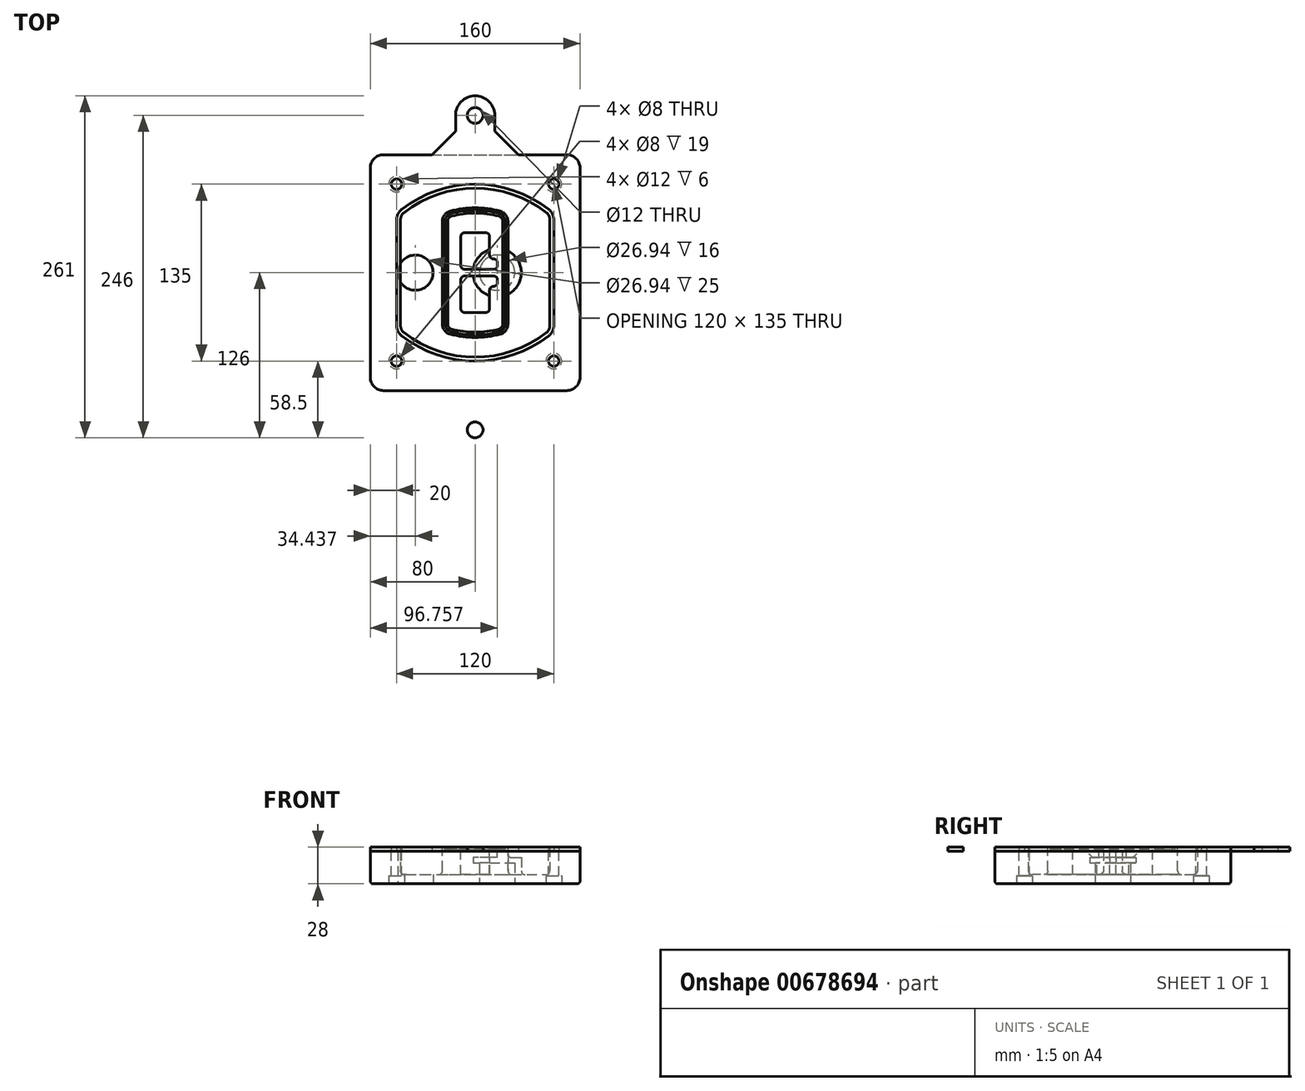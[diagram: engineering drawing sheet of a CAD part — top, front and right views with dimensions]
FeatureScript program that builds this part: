
annotation { "Feature Type Name" : "Feature", "Feature Type Description" : "" }
export const myFeature = defineFeature(function(context is Context, id is Id, definition is map)
    precondition{}
    {
        {
            var Q0;
            Q0=qCreatedBy(makeId("Top.planeOp"),FACE);
            var sketch = newSketch(context, id + "F0", { "sketchPlane" : qUnion([Q0])});
            skPoint(sketch, "E0.rect.middle", {"position": v(0, 0) * mm});
            skLineSegment(sketch, "E1.bottom", {"start": v(-70, -90) * mm, "end": v(70, -90) * mm});
            skLineSegment(sketch, "E1.top", {"start": v(-70, 90) * mm, "end": v(70, 90) * mm});
            skLineSegment(sketch, "E1.left", {"start": v(-80, -80) * mm, "end": v(-80, 80) * mm});
            skLineSegment(sketch, "E1.right", {"start": v(80, -80) * mm, "end": v(80, 80) * mm});
            skLineSegment(sketch, "E2", {"start": v(-80, 90) * mm, "end": v(80, -90) * mm, "construction": true});
            skLineSegment(sketch, "E3", {"start": v(80, 90) * mm, "end": v(-80, -90) * mm, "construction": true});
            skCircle(sketch, "E4", {"center": v(-60, 67.5) * mm, "radius": 4 * mm});
            skCircle(sketch, "E5", {"center": v(60, 67.5) * mm, "radius": 4 * mm});
            skCircle(sketch, "E6", {"center": v(60, -67.5) * mm, "radius": 4 * mm});
            skCircle(sketch, "E7", {"center": v(-60, -67.5) * mm, "radius": 4 * mm});
            skLineSegment(sketch, "E8", {"start": v(-60, 67.5) * mm, "end": v(60, 67.5) * mm, "construction": true});
            skLineSegment(sketch, "E9", {"start": v(60, 67.5) * mm, "end": v(60, -67.5) * mm, "construction": true});
            skLineSegment(sketch, "E10", {"start": v(60, -67.5) * mm, "end": v(-60, -67.5) * mm, "construction": true});
            skLineSegment(sketch, "E11", {"start": v(-60, -67.5) * mm, "end": v(-60, 67.5) * mm, "construction": true});
            skLineSegment(sketch, "E12", {"start": v(-60, 40.3) * mm, "end": v(-60, -40.3) * mm});
            skLineSegment(sketch, "E13", {"start": v(60, 40.3) * mm, "end": v(60, -40.3) * mm});
            skArc(sketch, "E14", {"start": v(56.15, 48.18) * mm, "mid": v(0, 67.5) * mm, "end": v(-56.15, 48.18) * mm});
            skArc(sketch, "E15", {"start": v(-56.15, -48.18) * mm, "mid": v(0, -67.5) * mm, "end": v(56.15, -48.18) * mm});
            skLineSegment(sketch, "E16", {"start": v(-60, 0) * mm, "end": v(60, 0) * mm, "construction": true});
            skPoint(sketch, "E17.visualSharp", {"position": v(-60, -45) * mm});
            skArc(sketch, "E17.filletArc", {"start": v(-60, -40.3) * mm, "mid": v(-58.99, -44.68) * mm, "end": v(-56.15, -48.18) * mm});
            skPoint(sketch, "E18.visualSharp", {"position": v(-60, 45) * mm});
            skArc(sketch, "E18.filletArc", {"start": v(-56.15, 48.18) * mm, "mid": v(-58.99, 44.68) * mm, "end": v(-60, 40.3) * mm});
            skPoint(sketch, "E19.visualSharp", {"position": v(60, 45) * mm});
            skArc(sketch, "E19.filletArc", {"start": v(60, 40.3) * mm, "mid": v(58.99, 44.68) * mm, "end": v(56.15, 48.18) * mm});
            skPoint(sketch, "E20.visualSharp", {"position": v(60, -45) * mm});
            skArc(sketch, "E20.filletArc", {"start": v(56.15, -48.18) * mm, "mid": v(58.99, -44.68) * mm, "end": v(60, -40.3) * mm});
            skPoint(sketch, "E21.visualSharp", {"position": v(-80, 90) * mm});
            skArc(sketch, "E21.filletArc", {"start": v(-70, 90) * mm, "mid": v(-77.07, 87.07) * mm, "end": v(-80, 80) * mm});
            skPoint(sketch, "E22.visualSharp", {"position": v(80, 90) * mm});
            skArc(sketch, "E22.filletArc", {"start": v(80, 80) * mm, "mid": v(77.07, 87.07) * mm, "end": v(70, 90) * mm});
            skPoint(sketch, "E23.visualSharp", {"position": v(80, -90) * mm});
            skArc(sketch, "E23.filletArc", {"start": v(70, -90) * mm, "mid": v(77.07, -87.07) * mm, "end": v(80, -80) * mm});
            skPoint(sketch, "E24.visualSharp", {"position": v(-80, -90) * mm});
            skArc(sketch, "E24.filletArc", {"start": v(-80, -80) * mm, "mid": v(-77.07, -87.07) * mm, "end": v(-70, -90) * mm});
            skArc(sketch, "E25.0", {"start": v(57, 40.3) * mm, "mid": v(56.3, 43.36) * mm, "end": v(54.3, 45.81) * mm});
            skLineSegment(sketch, "E25.1", {"start": v(57, 40.3) * mm, "end": v(57, -40.3) * mm});
            skArc(sketch, "E25.2", {"start": v(54.3, -45.81) * mm, "mid": v(56.3, -43.36) * mm, "end": v(57, -40.3) * mm});
            skArc(sketch, "E25.3", {"start": v(-54.3, -45.81) * mm, "mid": v(0, -64.5) * mm, "end": v(54.3, -45.81) * mm});
            skArc(sketch, "E25.4", {"start": v(-57, -40.3) * mm, "mid": v(-56.3, -43.36) * mm, "end": v(-54.3, -45.81) * mm});
            skArc(sketch, "E25.5", {"start": v(54.3, 45.81) * mm, "mid": v(0, 64.5) * mm, "end": v(-54.3, 45.81) * mm});
            skLineSegment(sketch, "E25.6", {"start": v(-57, 40.3) * mm, "end": v(-57, -40.3) * mm});
            skArc(sketch, "E25.7", {"start": v(-54.3, 45.81) * mm, "mid": v(-56.3, 43.36) * mm, "end": v(-57, 40.3) * mm});
            skArc(sketch, "E26.0", {"start": v(-58.62, 51.33) * mm, "mid": v(-62.58, 46.43) * mm, "end": v(-64, 40.3) * mm});
            skArc(sketch, "E26.1", {"start": v(58.62, 51.33) * mm, "mid": v(0, 71.5) * mm, "end": v(-58.62, 51.33) * mm});
            skArc(sketch, "E26.2", {"start": v(64, 40.3) * mm, "mid": v(62.58, 46.43) * mm, "end": v(58.62, 51.33) * mm});
            skLineSegment(sketch, "E26.3", {"start": v(64, 40.3) * mm, "end": v(64, -40.3) * mm});
            skArc(sketch, "E26.4", {"start": v(58.62, -51.33) * mm, "mid": v(62.58, -46.43) * mm, "end": v(64, -40.3) * mm});
            skLineSegment(sketch, "E26.5", {"start": v(-64, 40.3) * mm, "end": v(-64, -40.3) * mm});
            skArc(sketch, "E26.6", {"start": v(-58.62, -51.33) * mm, "mid": v(0, -71.5) * mm, "end": v(58.62, -51.33) * mm});
            skArc(sketch, "E26.7", {"start": v(-64, -40.3) * mm, "mid": v(-62.58, -46.43) * mm, "end": v(-58.62, -51.33) * mm});
            skSolve(sketch);
        }
        {
            var Q0;
            Q0=makeQuery(id+"F0.imprint","IMPRINT",FACE,{"disambiguationData":[TD([[makeQuery(id+"F0.imprint","IMPRINT",EDGE,{"derivedFrom":sQuery(id+"F0.wireOp",EDGE,"E1.bottom")}),1.0]])]});
            var Q1;
            Q1=makeQuery(id+"F0.imprint","IMPRINT",FACE,{"disambiguationData":[TD([[makeQuery(id+"F0.imprint","IMPRINT",EDGE,{"derivedFrom":sQuery(id+"F0.wireOp",EDGE,"E12")}),1.0]])]});
            var Q2;
            Q2=makeQuery(id+"F0.imprint","IMPRINT",FACE,{"disambiguationData":[TD([[makeQuery(id+"F0.imprint","IMPRINT",EDGE,{"derivedFrom":sQuery(id+"F0.wireOp",EDGE,"E25.0")}),1.0]])]});
            var Q3;
            Q3=makeQuery(id+"F0.imprint","IMPRINT",FACE,{"disambiguationData":[TD([[makeQuery(id+"F0.imprint","IMPRINT",EDGE,{"derivedFrom":sQuery(id+"F0.wireOp",EDGE,"E12")}),-1.0]])]});
            extrude(context, id + "F1", {"entities" : qUnion([Q0, Q1, Q2, Q3]), "oppositeDirection" : true, "depth" : 25 * mm});
        }
        {
            var Q0;
            Q0=makeQuery(id+"F0.imprint","IMPRINT",FACE,{"disambiguationData":[TD([[makeQuery(id+"F0.imprint","IMPRINT",EDGE,{"derivedFrom":sQuery(id+"F0.wireOp",EDGE,"E12")}),1.0]])]});
            extrude(context, id + "F2", {"entities" : qUnion([Q0]), "operationType" : NewBodyOperationType.ADD, "depth" : 3 * mm});
        }
        {
            var Q0;
            Q0=makeQuery(id+"F0.imprint","IMPRINT",FACE,{"disambiguationData":[TD([[makeQuery(id+"F0.imprint","IMPRINT",EDGE,{"derivedFrom":sQuery(id+"F0.wireOp",EDGE,"E25.0")}),1.0]])]});
            extrude(context, id + "F3", {"entities" : qUnion([Q0]), "operationType" : NewBodyOperationType.REMOVE, "oppositeDirection" : true, "depth" : 18 * mm});
        }
        {
            var Q0;
            Q0=makeQuery(id+"F2.opExtrude","CAP_FACE",FACE,{"disambiguationData":[OSD([sQuery(id+"F0.wireOp",EDGE,"E12"),sQuery(id+"F0.wireOp",EDGE,"E13"),sQuery(id+"F0.wireOp",EDGE,"E14"),sQuery(id+"F0.wireOp",EDGE,"E15"),sQuery(id+"F0.wireOp",EDGE,"E17.filletArc"),sQuery(id+"F0.wireOp",EDGE,"E18.filletArc"),sQuery(id+"F0.wireOp",EDGE,"E19.filletArc"),sQuery(id+"F0.wireOp",EDGE,"E20.filletArc"),sQuery(id+"F0.wireOp",EDGE,"E25.0"),sQuery(id+"F0.wireOp",EDGE,"E25.1"),sQuery(id+"F0.wireOp",EDGE,"E25.2"),sQuery(id+"F0.wireOp",EDGE,"E25.3"),sQuery(id+"F0.wireOp",EDGE,"E25.4"),sQuery(id+"F0.wireOp",EDGE,"E25.5"),sQuery(id+"F0.wireOp",EDGE,"E25.6"),sQuery(id+"F0.wireOp",EDGE,"E25.7")])],"isStart":false});
            var sketch = newSketch(context, id + "F4", { "sketchPlane" : qUnion([Q0])});
            skArc(sketch, "E27.0", {"start": v(-19.08, -46.97) * mm, "mid": v(0, -49.5) * mm, "end": v(19.08, -46.97) * mm});
            skArc(sketch, "E28.0", {"start": v(19.08, 46.97) * mm, "mid": v(0, 49.5) * mm, "end": v(-19.08, 46.97) * mm});
            skLineSegment(sketch, "E29", {"start": v(-25, 39.25) * mm, "end": v(-25, -39.25) * mm});
            skLineSegment(sketch, "E30", {"start": v(25, 39.25) * mm, "end": v(25, -39.25) * mm});
            skLineSegment(sketch, "E31", {"start": v(-25, 45.1) * mm, "end": v(25, 45.1) * mm, "construction": true});
            skLineSegment(sketch, "E32", {"start": v(-25, -45.1) * mm, "end": v(25, -45.1) * mm, "construction": true});
            skPoint(sketch, "E33.visualSharp", {"position": v(-25, 45.1) * mm});
            skArc(sketch, "E33.filletArc", {"start": v(-19.08, 46.97) * mm, "mid": v(-23.35, 44.11) * mm, "end": v(-25, 39.25) * mm});
            skPoint(sketch, "E34.visualSharp", {"position": v(25, 45.1) * mm});
            skArc(sketch, "E34.filletArc", {"start": v(25, 39.25) * mm, "mid": v(23.35, 44.11) * mm, "end": v(19.08, 46.97) * mm});
            skPoint(sketch, "E35.visualSharp", {"position": v(25, -45.1) * mm});
            skArc(sketch, "E35.filletArc", {"start": v(19.08, -46.97) * mm, "mid": v(23.35, -44.11) * mm, "end": v(25, -39.25) * mm});
            skPoint(sketch, "E36.visualSharp", {"position": v(-25, -45.1) * mm});
            skArc(sketch, "E36.filletArc", {"start": v(-25, -39.25) * mm, "mid": v(-23.35, -44.11) * mm, "end": v(-19.08, -46.97) * mm});
            skArc(sketch, "E37.0", {"start": v(54.3, 45.81) * mm, "mid": v(0, 64.5) * mm, "end": v(-54.3, 45.81) * mm});
            skArc(sketch, "E37.1", {"start": v(-54.3, 45.81) * mm, "mid": v(-56.3, 43.36) * mm, "end": v(-57, 40.3) * mm});
            skLineSegment(sketch, "E37.2", {"start": v(-57, 40.3) * mm, "end": v(-57, -40.3) * mm});
            skArc(sketch, "E37.3", {"start": v(-57, -40.3) * mm, "mid": v(-56.3, -43.36) * mm, "end": v(-54.3, -45.81) * mm});
            skArc(sketch, "E37.4", {"start": v(-54.3, -45.81) * mm, "mid": v(0, -64.5) * mm, "end": v(54.3, -45.81) * mm});
            skArc(sketch, "E37.5", {"start": v(54.3, -45.81) * mm, "mid": v(56.3, -43.36) * mm, "end": v(57, -40.3) * mm});
            skLineSegment(sketch, "E37.6", {"start": v(57, 40.3) * mm, "end": v(57, -40.3) * mm});
            skArc(sketch, "E37.7", {"start": v(57, 40.3) * mm, "mid": v(56.3, 43.36) * mm, "end": v(54.3, 45.81) * mm});
            skLineSegment(sketch, "E38.0", {"start": v(23, 39.25) * mm, "end": v(23, -39.25) * mm});
            skArc(sketch, "E38.1", {"start": v(18.56, -45.04) * mm, "mid": v(21.76, -42.9) * mm, "end": v(23, -39.25) * mm});
            skArc(sketch, "E38.2", {"start": v(-18.56, -45.04) * mm, "mid": v(0, -47.5) * mm, "end": v(18.56, -45.04) * mm});
            skArc(sketch, "E38.3", {"start": v(-23, -39.25) * mm, "mid": v(-21.76, -42.9) * mm, "end": v(-18.56, -45.04) * mm});
            skLineSegment(sketch, "E38.4", {"start": v(-23, 39.25) * mm, "end": v(-23, -39.25) * mm});
            skArc(sketch, "E38.5", {"start": v(23, 39.25) * mm, "mid": v(21.76, 42.9) * mm, "end": v(18.56, 45.04) * mm});
            skArc(sketch, "E38.6", {"start": v(-18.56, 45.04) * mm, "mid": v(-21.76, 42.9) * mm, "end": v(-23, 39.25) * mm});
            skArc(sketch, "E38.7", {"start": v(18.56, 45.04) * mm, "mid": v(0, 47.5) * mm, "end": v(-18.56, 45.04) * mm});
            skArc(sketch, "E39.0", {"start": v(21, 39.25) * mm, "mid": v(20.18, 41.68) * mm, "end": v(18.04, 43.1) * mm});
            skLineSegment(sketch, "E39.1", {"start": v(21, 39.25) * mm, "end": v(21, -39.25) * mm});
            skArc(sketch, "E39.2", {"start": v(18.04, -43.1) * mm, "mid": v(20.18, -41.68) * mm, "end": v(21, -39.25) * mm});
            skArc(sketch, "E39.3", {"start": v(-18.04, -43.1) * mm, "mid": v(0, -45.5) * mm, "end": v(18.04, -43.1) * mm});
            skArc(sketch, "E39.4", {"start": v(-21, -39.25) * mm, "mid": v(-20.18, -41.68) * mm, "end": v(-18.04, -43.1) * mm});
            skArc(sketch, "E39.5", {"start": v(18.04, 43.1) * mm, "mid": v(0, 45.5) * mm, "end": v(-18.04, 43.1) * mm});
            skLineSegment(sketch, "E39.6", {"start": v(-21, 39.25) * mm, "end": v(-21, -39.25) * mm});
            skArc(sketch, "E39.7", {"start": v(-18.04, 43.1) * mm, "mid": v(-20.18, 41.68) * mm, "end": v(-21, 39.25) * mm});
            skLineSegment(sketch, "E40", {"start": v(-25, 0) * mm, "end": v(25, 0) * mm, "construction": true});
            skLineSegment(sketch, "E41", {"start": v(-11, 5.5) * mm, "end": v(-11, 27.5) * mm});
            skLineSegment(sketch, "E42", {"start": v(-8, 30.5) * mm, "end": v(8, 30.5) * mm});
            skLineSegment(sketch, "E43", {"start": v(11, 27.5) * mm, "end": v(11, 13.5) * mm});
            skLineSegment(sketch, "E44", {"start": v(14, 10.5) * mm, "end": v(14, 10.5) * mm});
            skLineSegment(sketch, "E45", {"start": v(17, 7.5) * mm, "end": v(17, 5.5) * mm});
            skLineSegment(sketch, "E46", {"start": v(14, 2.5) * mm, "end": v(-8, 2.5) * mm});
            skPoint(sketch, "E47.visualSharp", {"position": v(-11, 30.5) * mm});
            skArc(sketch, "E47.filletArc", {"start": v(-8, 30.5) * mm, "mid": v(-10.12, 29.62) * mm, "end": v(-11, 27.5) * mm});
            skPoint(sketch, "E48.visualSharp", {"position": v(11, 30.5) * mm});
            skArc(sketch, "E48.filletArc", {"start": v(11, 27.5) * mm, "mid": v(10.12, 29.62) * mm, "end": v(8, 30.5) * mm});
            skPoint(sketch, "E49.visualSharp", {"position": v(11, 10.5) * mm});
            skArc(sketch, "E49.filletArc", {"start": v(11, 13.5) * mm, "mid": v(11.88, 11.38) * mm, "end": v(14, 10.5) * mm});
            skPoint(sketch, "E50.visualSharp", {"position": v(17, 10.5) * mm});
            skArc(sketch, "E50.filletArc", {"start": v(17, 7.5) * mm, "mid": v(16.12, 9.62) * mm, "end": v(14, 10.5) * mm});
            skPoint(sketch, "E51.visualSharp", {"position": v(17, 2.5) * mm});
            skArc(sketch, "E51.filletArc", {"start": v(14, 2.5) * mm, "mid": v(16.12, 3.38) * mm, "end": v(17, 5.5) * mm});
            skPoint(sketch, "E52.visualSharp", {"position": v(-11, 2.5) * mm});
            skArc(sketch, "E52.filletArc", {"start": v(-11, 5.5) * mm, "mid": v(-10.12, 3.38) * mm, "end": v(-8, 2.5) * mm});
            skLineSegment(sketch, "E53.0.MirrorCS", {"start": v(14, -2.5) * mm, "end": v(-8, -2.5) * mm});
            skArc(sketch, "E54.0.MirrorCS", {"start": v(-11, -5.5) * mm, "mid": v(-10.12, -3.38) * mm, "end": v(-8, -2.5) * mm});
            skLineSegment(sketch, "E55.0.MirrorCS", {"start": v(-11, -5.5) * mm, "end": v(-11, -27.5) * mm});
            skArc(sketch, "E56.0.MirrorCS", {"start": v(-8, -30.5) * mm, "mid": v(-10.12, -29.62) * mm, "end": v(-11, -27.5) * mm});
            skLineSegment(sketch, "E57.0.MirrorCS", {"start": v(-8, -30.5) * mm, "end": v(8, -30.5) * mm});
            skArc(sketch, "E58.0.MirrorCS", {"start": v(11, -27.5) * mm, "mid": v(10.12, -29.62) * mm, "end": v(8, -30.5) * mm});
            skLineSegment(sketch, "E59.0.MirrorCS", {"start": v(11, -27.5) * mm, "end": v(11, -13.5) * mm});
            skArc(sketch, "E60.0.MirrorCS", {"start": v(11, -13.5) * mm, "mid": v(11.88, -11.38) * mm, "end": v(14, -10.5) * mm});
            skArc(sketch, "E61.0.MirrorCS", {"start": v(17, -7.5) * mm, "mid": v(16.12, -9.62) * mm, "end": v(14, -10.5) * mm});
            skLineSegment(sketch, "E62.0.MirrorCS", {"start": v(17, -7.5) * mm, "end": v(17, -5.5) * mm});
            skArc(sketch, "E63.0.MirrorCS", {"start": v(14, -2.5) * mm, "mid": v(16.12, -3.38) * mm, "end": v(17, -5.5) * mm});
            skSolve(sketch);
        }
        {
            var Q0;
            Q0=makeQuery(id+"F4.imprint","IMPRINT",FACE,{"disambiguationData":[TD([[makeQuery(id+"F4.imprint","IMPRINT",EDGE,{"derivedFrom":sQuery(id+"F4.wireOp",EDGE,"E27.0")}),1.0]])]});
            var Q1;
            Q1=makeQuery(id+"F4.imprint","IMPRINT",FACE,{"disambiguationData":[TD([[makeQuery(id+"F4.imprint","IMPRINT",EDGE,{"derivedFrom":sQuery(id+"F4.wireOp",EDGE,"E38.0")}),-1.0]])]});
            var Q2;
            Q2=makeQuery(id+"F4.imprint","IMPRINT",FACE,{"disambiguationData":[TD([[makeQuery(id+"F4.imprint","IMPRINT",EDGE,{"derivedFrom":sQuery(id+"F4.wireOp",EDGE,"E39.0")}),1.0]])]});
            extrude(context, id + "F5", {"entities" : qUnion([Q0, Q1, Q2]), "operationType" : NewBodyOperationType.ADD, "endBound" : BoundingType.UP_TO_NEXT, "oppositeDirection" : true, "depth" : 25 * mm});
        }
        {
            var Q0;
            Q0=makeQuery(id+"F4.imprint","IMPRINT",FACE,{"disambiguationData":[TD([[makeQuery(id+"F4.imprint","IMPRINT",EDGE,{"derivedFrom":sQuery(id+"F4.wireOp",EDGE,"E38.0")}),-1.0]])]});
            extrude(context, id + "F6", {"entities" : qUnion([Q0]), "operationType" : NewBodyOperationType.REMOVE, "oppositeDirection" : true, "depth" : 2 * mm});
        }
        {
            var Q0;
            Q0=makeQuery(id+"F1.opExtrude","CAP_FACE",FACE,{"disambiguationData":[OSD([sQuery(id+"F0.wireOp",EDGE,"E1.bottom"),sQuery(id+"F0.wireOp",EDGE,"E1.top"),sQuery(id+"F0.wireOp",EDGE,"E1.left"),sQuery(id+"F0.wireOp",EDGE,"E1.right"),sQuery(id+"F0.wireOp",EDGE,"E4"),sQuery(id+"F0.wireOp",EDGE,"E5"),sQuery(id+"F0.wireOp",EDGE,"E6"),sQuery(id+"F0.wireOp",EDGE,"E7"),sQuery(id+"F0.wireOp",EDGE,"E21.filletArc"),sQuery(id+"F0.wireOp",EDGE,"E22.filletArc"),sQuery(id+"F0.wireOp",EDGE,"E23.filletArc"),sQuery(id+"F0.wireOp",EDGE,"E24.filletArc")])],"isStart":false});
            var sketch = newSketch(context, id + "F7", { "sketchPlane" : qUnion([Q0])});
            skCircle(sketch, "E64", {"center": v(16.76, 0) * mm, "radius": 13.47 * mm});
            skCircle(sketch, "E65", {"center": v(-45.56, 0) * mm, "radius": 13.47 * mm});
            skLineSegment(sketch, "E66", {"start": v(80, 0) * mm, "end": v(-80, 0) * mm});
            skCircle(sketch, "E67", {"center": v(16.76, 0) * mm, "radius": 18.47 * mm});
            skCircle(sketch, "E68", {"center": v(60, -67.5) * mm, "radius": 6 * mm});
            skCircle(sketch, "E69", {"center": v(-60, -67.5) * mm, "radius": 6 * mm});
            skCircle(sketch, "E70", {"center": v(-60, 67.5) * mm, "radius": 6 * mm});
            skCircle(sketch, "E71", {"center": v(60, 67.5) * mm, "radius": 6 * mm});
            skSolve(sketch);
        }
        {
            var Q0;
            {var subQ1=sQuery(id+"F7.wireOp",EDGE,"E66");var subQ4=sQuery(id+"F7.wireOp",EDGE,"E64");var subQ6=makeQuery(id+"F7.imprint","INTERSECT",VERTEX,{"disambiguationData":[OD(0.0)],"derivedFrom":[subQ4,subQ1]});Q0=makeQuery(id+"F7.imprint","IMPRINT",FACE,{"disambiguationData":[TD([[makeQuery(id+"F7.imprint","IMPRINT",EDGE,{"disambiguationData":[TD([[subQ6,-1.0]])],"derivedFrom":subQ4}),-1.0]])]});}
            var Q1;
            {var subQ0=sQuery(id+"F7.wireOp",EDGE,"E66");var subQ1=sQuery(id+"F7.wireOp",EDGE,"E64");var subQ3=makeQuery(id+"F7.imprint","INTERSECT",VERTEX,{"disambiguationData":[OD(0.0)],"derivedFrom":[subQ1,subQ0]});Q1=makeQuery(id+"F7.imprint","IMPRINT",FACE,{"disambiguationData":[TD([[makeQuery(id+"F7.imprint","IMPRINT",EDGE,{"disambiguationData":[TD([[subQ3,-1.0]])],"derivedFrom":subQ1}),1.0]])]});}
            var Q2;
            {var subQ0=sQuery(id+"F7.wireOp",EDGE,"E66");var subQ1=sQuery(id+"F7.wireOp",EDGE,"E64");var subQ3=makeQuery(id+"F7.imprint","INTERSECT",VERTEX,{"disambiguationData":[OD(0.0)],"derivedFrom":[subQ1,subQ0]});Q2=makeQuery(id+"F7.imprint","IMPRINT",FACE,{"disambiguationData":[TD([[makeQuery(id+"F7.imprint","IMPRINT",EDGE,{"disambiguationData":[TD([[subQ3,1.0]])],"derivedFrom":subQ1}),1.0]])]});}
            var Q3;
            {var subQ1=sQuery(id+"F7.wireOp",EDGE,"E66");var subQ4=sQuery(id+"F7.wireOp",EDGE,"E64");var subQ6=makeQuery(id+"F7.imprint","INTERSECT",VERTEX,{"disambiguationData":[OD(0.0)],"derivedFrom":[subQ4,subQ1]});Q3=makeQuery(id+"F7.imprint","IMPRINT",FACE,{"disambiguationData":[TD([[makeQuery(id+"F7.imprint","IMPRINT",EDGE,{"disambiguationData":[TD([[subQ6,1.0]])],"derivedFrom":subQ4}),-1.0]])]});}
            extrude(context, id + "F8", {"entities" : qUnion([Q0, Q1, Q2, Q3]), "operationType" : NewBodyOperationType.ADD, "oppositeDirection" : true, "depth" : 20 * mm});
        }
        {
            var Q0;
            {var subQ0=sQuery(id+"F7.wireOp",EDGE,"E66");var subQ1=sQuery(id+"F7.wireOp",EDGE,"E64");var subQ3=makeQuery(id+"F7.imprint","INTERSECT",VERTEX,{"disambiguationData":[OD(0.0)],"derivedFrom":[subQ1,subQ0]});Q0=makeQuery(id+"F7.imprint","IMPRINT",FACE,{"disambiguationData":[TD([[makeQuery(id+"F7.imprint","IMPRINT",EDGE,{"disambiguationData":[TD([[subQ3,-1.0]])],"derivedFrom":subQ1}),1.0]])]});}
            var Q1;
            {var subQ0=sQuery(id+"F7.wireOp",EDGE,"E66");var subQ1=sQuery(id+"F7.wireOp",EDGE,"E64");var subQ3=makeQuery(id+"F7.imprint","INTERSECT",VERTEX,{"disambiguationData":[OD(0.0)],"derivedFrom":[subQ1,subQ0]});Q1=makeQuery(id+"F7.imprint","IMPRINT",FACE,{"disambiguationData":[TD([[makeQuery(id+"F7.imprint","IMPRINT",EDGE,{"disambiguationData":[TD([[subQ3,1.0]])],"derivedFrom":subQ1}),1.0]])]});}
            extrude(context, id + "F9", {"entities" : qUnion([Q0, Q1]), "operationType" : NewBodyOperationType.REMOVE, "oppositeDirection" : true, "depth" : 16 * mm});
        }
        {
            var Q0;
            {var subQ0=sQuery(id+"F7.wireOp",EDGE,"E66");var subQ1=sQuery(id+"F7.wireOp",EDGE,"E65");var subQ3=makeQuery(id+"F7.imprint","INTERSECT",VERTEX,{"disambiguationData":[OD(0.0)],"derivedFrom":[subQ1,subQ0]});Q0=makeQuery(id+"F7.imprint","IMPRINT",FACE,{"disambiguationData":[TD([[makeQuery(id+"F7.imprint","IMPRINT",EDGE,{"disambiguationData":[TD([[subQ3,-1.0]])],"derivedFrom":subQ1}),1.0]])]});}
            var Q1;
            {var subQ0=sQuery(id+"F7.wireOp",EDGE,"E66");var subQ1=sQuery(id+"F7.wireOp",EDGE,"E65");var subQ3=makeQuery(id+"F7.imprint","INTERSECT",VERTEX,{"disambiguationData":[OD(0.0)],"derivedFrom":[subQ1,subQ0]});Q1=makeQuery(id+"F7.imprint","IMPRINT",FACE,{"disambiguationData":[TD([[makeQuery(id+"F7.imprint","IMPRINT",EDGE,{"disambiguationData":[TD([[subQ3,1.0]])],"derivedFrom":subQ1}),1.0]])]});}
            extrude(context, id + "F10", {"entities" : qUnion([Q0, Q1]), "operationType" : NewBodyOperationType.REMOVE, "oppositeDirection" : true, "depth" : 25 * mm});
        }
        {
            var Q0;
            Q0=makeQuery(id+"F7.imprint","IMPRINT",FACE,{"disambiguationData":[TD([[makeQuery(id+"F7.imprint","IMPRINT",EDGE,{"derivedFrom":sQuery(id+"F7.wireOp",EDGE,"E68")}),1.0]])]});
            var Q1;
            Q1=makeQuery(id+"F7.imprint","IMPRINT",FACE,{"disambiguationData":[TD([[makeQuery(id+"F7.imprint","IMPRINT",EDGE,{"derivedFrom":makeQuery(id+"F1.opExtrude","CAP_EDGE",EDGE,{"disambiguationData":[OSD([sQuery(id+"F0.wireOp",EDGE,"E5")])],"isStart":false})}),-1.0]])]});
            var Q2;
            Q2=makeQuery(id+"F7.imprint","IMPRINT",FACE,{"disambiguationData":[TD([[makeQuery(id+"F7.imprint","IMPRINT",EDGE,{"derivedFrom":sQuery(id+"F7.wireOp",EDGE,"E69")}),1.0]])]});
            var Q3;
            Q3=makeQuery(id+"F7.imprint","IMPRINT",FACE,{"disambiguationData":[TD([[makeQuery(id+"F7.imprint","IMPRINT",EDGE,{"derivedFrom":makeQuery(id+"F1.opExtrude","CAP_EDGE",EDGE,{"disambiguationData":[OSD([sQuery(id+"F0.wireOp",EDGE,"E4")])],"isStart":false})}),-1.0]])]});
            var Q4;
            Q4=makeQuery(id+"F7.imprint","IMPRINT",FACE,{"disambiguationData":[TD([[makeQuery(id+"F7.imprint","IMPRINT",EDGE,{"derivedFrom":sQuery(id+"F7.wireOp",EDGE,"E70")}),1.0]])]});
            var Q5;
            Q5=makeQuery(id+"F7.imprint","IMPRINT",FACE,{"disambiguationData":[TD([[makeQuery(id+"F7.imprint","IMPRINT",EDGE,{"derivedFrom":makeQuery(id+"F1.opExtrude","CAP_EDGE",EDGE,{"disambiguationData":[OSD([sQuery(id+"F0.wireOp",EDGE,"E7")])],"isStart":false})}),-1.0]])]});
            var Q6;
            Q6=makeQuery(id+"F7.imprint","IMPRINT",FACE,{"disambiguationData":[TD([[makeQuery(id+"F7.imprint","IMPRINT",EDGE,{"derivedFrom":sQuery(id+"F7.wireOp",EDGE,"E71")}),1.0]])]});
            var Q7;
            Q7=makeQuery(id+"F7.imprint","IMPRINT",FACE,{"disambiguationData":[TD([[makeQuery(id+"F7.imprint","IMPRINT",EDGE,{"derivedFrom":makeQuery(id+"F1.opExtrude","CAP_EDGE",EDGE,{"disambiguationData":[OSD([sQuery(id+"F0.wireOp",EDGE,"E6")])],"isStart":false})}),-1.0]])]});
            extrude(context, id + "F11", {"entities" : qUnion([Q0, Q1, Q2, Q3, Q4, Q5, Q6, Q7]), "operationType" : NewBodyOperationType.REMOVE, "oppositeDirection" : true, "depth" : 6 * mm});
        }
        {
            var Q0;
            Q0=makeQuery(id+"F9.boolean.opBoolean","COPY",FACE,{"derivedFrom":makeQuery(id+"F9.opExtrude","CAP_FACE",FACE,{"disambiguationData":[OSD([sQuery(id+"F7.wireOp",EDGE,"E64")])],"isStart":false})});
            var sketch = newSketch(context, id + "F12", { "sketchPlane" : qUnion([Q0])});
            skArc(sketch, "E72.0", {"start": v(11, 17.55) * mm, "mid": v(2.57, 11.82) * mm, "end": v(-1.54, 2.5) * mm});
            skArc(sketch, "E72.1", {"start": v(-1.54, -2.5) * mm, "mid": v(2.57, -11.82) * mm, "end": v(11, -17.55) * mm});
            skLineSegment(sketch, "E73", {"start": v(-1.54, -2.5) * mm, "end": v(14, -2.5) * mm});
            skLineSegment(sketch, "E74.0", {"start": v(14, 2.5) * mm, "end": v(-1.54, 2.5) * mm});
            skArc(sketch, "E74.1", {"start": v(14, 2.5) * mm, "mid": v(16.12, 3.38) * mm, "end": v(17, 5.5) * mm});
            skLineSegment(sketch, "E74.2", {"start": v(17, 7.5) * mm, "end": v(17, 5.5) * mm});
            skArc(sketch, "E74.3", {"start": v(17, 7.5) * mm, "mid": v(16.12, 9.62) * mm, "end": v(14, 10.5) * mm});
            skArc(sketch, "E74.4", {"start": v(11, 13.5) * mm, "mid": v(11.88, 11.38) * mm, "end": v(14, 10.5) * mm});
            skLineSegment(sketch, "E74.5", {"start": v(11, 17.55) * mm, "end": v(11, 13.5) * mm});
            skLineSegment(sketch, "E74.7", {"start": v(14, -2.5) * mm, "end": v(-1.54, -2.5) * mm});
            skArc(sketch, "E74.8", {"start": v(14, -2.5) * mm, "mid": v(16.12, -3.38) * mm, "end": v(17, -5.5) * mm});
            skLineSegment(sketch, "E74.9", {"start": v(17, -7.5) * mm, "end": v(17, -5.5) * mm});
            skArc(sketch, "E74.10", {"start": v(17, -7.5) * mm, "mid": v(16.12, -9.62) * mm, "end": v(14, -10.5) * mm});
            skArc(sketch, "E74.11", {"start": v(11, -13.5) * mm, "mid": v(11.88, -11.38) * mm, "end": v(14, -10.5) * mm});
            skLineSegment(sketch, "E74.12", {"start": v(11, -17.55) * mm, "end": v(11, -13.5) * mm});
            skPoint(sketch, "E75.orphan", {"position": v(11, -27.5) * mm});
            skPoint(sketch, "E76.orphan", {"position": v(-8, -2.5) * mm});
            skPoint(sketch, "E77.orphan", {"position": v(-8, 2.5) * mm});
            skPoint(sketch, "E78.orphan", {"position": v(11, 27.5) * mm});
            skSolve(sketch);
        }
        {
            var Q0;
            {var subQ7=sQuery(id+"F12.wireOp",EDGE,"E72.0");var subQ14=sQuery(id+"F12.wireOp",EDGE,"E72.1");var subQ16=sQuery(id+"F12.wireOp",EDGE,"E74.1");var subQ18=sQuery(id+"F12.wireOp",EDGE,"E74.8");Q0=qUnion([makeQuery(id+"F12.imprint","IMPRINT",FACE,{"disambiguationData":[TD([[makeQuery(id+"F12.imprint","IMPRINT",EDGE,{"derivedFrom":subQ7}),1.0]])]}),makeQuery(id+"F12.imprint","IMPRINT",FACE,{"disambiguationData":[TD([[makeQuery(id+"F12.imprint","IMPRINT",EDGE,{"derivedFrom":subQ14}),1.0]])]}),makeQuery(id+"F12.imprint","IMPRINT",FACE,{"disambiguationData":[TD([[makeQuery(id+"F12.imprint","IMPRINT",EDGE,{"derivedFrom":subQ16}),1.0]])]}),makeQuery(id+"F12.imprint","IMPRINT",FACE,{"disambiguationData":[TD([[makeQuery(id+"F12.imprint","IMPRINT",EDGE,{"derivedFrom":subQ18}),-1.0]])]})]);}
            var Q1;
            Q1=makeQuery(id+"F5.boolean.opBoolean","SPLIT",FACE,{"disambiguationData":[TD([makeQuery(id+"F5.opExtrude","SWEPT_FACE",FACE,{"disambiguationData":[OSD([sQuery(id+"F4.wireOp",EDGE,"E41")])]})])],"derivedFrom":makeQuery(id+"F3.boolean.opBoolean","COPY",FACE,{"derivedFrom":makeQuery(id+"F3.opExtrude","CAP_FACE",FACE,{"disambiguationData":[OSD([sQuery(id+"F0.wireOp",EDGE,"E25.0"),sQuery(id+"F0.wireOp",EDGE,"E25.1"),sQuery(id+"F0.wireOp",EDGE,"E25.2"),sQuery(id+"F0.wireOp",EDGE,"E25.3"),sQuery(id+"F0.wireOp",EDGE,"E25.4"),sQuery(id+"F0.wireOp",EDGE,"E25.5"),sQuery(id+"F0.wireOp",EDGE,"E25.6"),sQuery(id+"F0.wireOp",EDGE,"E25.7")])],"isStart":false})})});
            extrude(context, id + "F13", {"entities" : qUnion([Q0]), "operationType" : NewBodyOperationType.REMOVE, "endBound" : BoundingType.UP_TO_SURFACE, "endBoundEntityFace" : qUnion([Q1]), "depth" : 25 * mm});
        }
        {
            var Q0;
            Q0=makeQuery(id+"F3.boolean.opBoolean","COPY",EDGE,{"derivedFrom":makeQuery(id+"F3.opExtrude","CAP_EDGE",EDGE,{"disambiguationData":[OSD([sQuery(id+"F0.wireOp",EDGE,"E25.6")])],"isStart":false})});
            var Q1;
            Q1=makeQuery(id+"F8.boolean.opBoolean","INTERSECT",EDGE,{"derivedFrom":[makeQuery(id+"F5.opExtrude","SWEPT_FACE",FACE,{"disambiguationData":[OSD([sQuery(id+"F4.wireOp",EDGE,"E30")])]}),makeQuery(id+"F8.opExtrude","CAP_FACE",FACE,{"disambiguationData":[OSD([sQuery(id+"F7.wireOp",EDGE,"E67")])],"isStart":false})]});
            var Q2;
            Q2=makeQuery(id+"F8.boolean.opBoolean","INTERSECT",EDGE,{"disambiguationData":[OD(1.0)],"derivedFrom":[makeQuery(id+"F5.opExtrude","SWEPT_FACE",FACE,{"disambiguationData":[OSD([sQuery(id+"F4.wireOp",EDGE,"E30")])]}),makeQuery(id+"F8.opExtrude","SWEPT_FACE",FACE,{"disambiguationData":[OSD([sQuery(id+"F7.wireOp",EDGE,"E67")])]})]});
            var Q3;
            {var subQ0=sQuery(id+"F4.wireOp",EDGE,"E30");Q3=makeQuery(id+"F8.boolean.opBoolean","SPLIT",EDGE,{"disambiguationData":[TD([makeQuery(id+"F5.opExtrude","SWEPT_FACE",FACE,{"disambiguationData":[OSD([sQuery(id+"F4.wireOp",EDGE,"E35.filletArc")])]})])],"derivedFrom":makeQuery(id+"F5.opExtrude","CAP_EDGE",EDGE,{"disambiguationData":[OSD([subQ0])],"isStart":false})});}
            var Q4;
            {var subQ0=sQuery(id+"F0.wireOp",EDGE,"E25.7");var subQ1=sQuery(id+"F0.wireOp",EDGE,"E25.1");var subQ2=sQuery(id+"F0.wireOp",EDGE,"E25.6");var subQ3=sQuery(id+"F0.wireOp",EDGE,"E25.5");var subQ4=sQuery(id+"F0.wireOp",EDGE,"E25.4");var subQ5=sQuery(id+"F0.wireOp",EDGE,"E25.0");var subQ6=sQuery(id+"F0.wireOp",EDGE,"E25.2");var subQ7=sQuery(id+"F0.wireOp",EDGE,"E25.3");Q4=makeQuery(id+"F8.boolean.opBoolean","INTERSECT",EDGE,{"derivedFrom":[makeQuery(id+"F5.boolean.opBoolean","SPLIT",FACE,{"disambiguationData":[TD([makeQuery(id+"F2.opExtrude","SWEPT_FACE",FACE,{"disambiguationData":[OSD([subQ5])]})])],"derivedFrom":makeQuery(id+"F3.boolean.opBoolean","COPY",FACE,{"derivedFrom":makeQuery(id+"F3.opExtrude","CAP_FACE",FACE,{"disambiguationData":[OSD([subQ5,subQ1,subQ6,subQ7,subQ4,subQ3,subQ2,subQ0])],"isStart":false})})}),makeQuery(id+"F8.opExtrude","SWEPT_FACE",FACE,{"disambiguationData":[OSD([sQuery(id+"F7.wireOp",EDGE,"E67")])]})]});}
            var Q5;
            Q5=makeQuery(id+"F8.boolean.opBoolean","INTERSECT",EDGE,{"disambiguationData":[OD(0.0)],"derivedFrom":[makeQuery(id+"F5.opExtrude","SWEPT_FACE",FACE,{"disambiguationData":[OSD([sQuery(id+"F4.wireOp",EDGE,"E30")])]}),makeQuery(id+"F8.opExtrude","SWEPT_FACE",FACE,{"disambiguationData":[OSD([sQuery(id+"F7.wireOp",EDGE,"E67")])]})]});
            fillet(context, id + "F14", {"entities" : qUnion([Q0, Q1, Q2, Q3, Q4, Q5]), "radius" : 3 * mm, "tangentPropagation" : true, "allowEdgeOverflow" : false});
        }
        {
            var Q0;
            Q0=makeQuery(id+"F1.opExtrude","CAP_EDGE",EDGE,{"disambiguationData":[OSD([sQuery(id+"F0.wireOp",EDGE,"E1.bottom")])],"isStart":false});
            fillet(context, id + "F15", {"entities" : qUnion([Q0]), "radius" : 2 * mm, "tangentPropagation" : true, "allowEdgeOverflow" : false});
        }
        {
            var Q0;
            {var subQ0=sQuery(id+"F0.wireOp",EDGE,"E21.filletArc");var subQ1=sQuery(id+"F0.wireOp",EDGE,"E7");var subQ2=sQuery(id+"F0.wireOp",EDGE,"E6");var subQ3=sQuery(id+"F0.wireOp",EDGE,"E5");var subQ4=sQuery(id+"F0.wireOp",EDGE,"E4");var subQ5=sQuery(id+"F0.wireOp",EDGE,"E22.filletArc");var subQ6=sQuery(id+"F0.wireOp",EDGE,"E1.bottom");var subQ7=sQuery(id+"F0.wireOp",EDGE,"E1.right");var subQ8=sQuery(id+"F0.wireOp",EDGE,"E1.top");var subQ9=sQuery(id+"F0.wireOp",EDGE,"E1.left");var subQ10=sQuery(id+"F0.wireOp",EDGE,"E23.filletArc");var subQ11=sQuery(id+"F0.wireOp",EDGE,"E24.filletArc");Q0=makeQuery(id+"F2.boolean.opBoolean","SPLIT",FACE,{"disambiguationData":[TD([makeQuery(id+"F1.opExtrude","SWEPT_FACE",FACE,{"disambiguationData":[OSD([subQ6])]})])],"derivedFrom":makeQuery(id+"F1.opExtrude","CAP_FACE",FACE,{"disambiguationData":[OSD([subQ6,subQ8,subQ9,subQ7,subQ4,subQ3,subQ2,subQ1,subQ0,subQ5,subQ10,subQ11])],"isStart":true})});}
            var sketch = newSketch(context, id + "F16", { "sketchPlane" : qUnion([Q0])});
            skCircle(sketch, "E79", {"center": v(0, 120) * mm, "radius": 6 * mm});
            skLineSegment(sketch, "E80", {"start": v(33, 90) * mm, "end": v(15, 108) * mm});
            skLineSegment(sketch, "E81", {"start": v(15, 108) * mm, "end": v(15, 120) * mm});
            skLineSegment(sketch, "E82", {"start": v(-33, 90) * mm, "end": v(-15, 108) * mm});
            skLineSegment(sketch, "E83", {"start": v(-15, 108) * mm, "end": v(-15, 120) * mm});
            skArc(sketch, "E84", {"start": v(15, 120) * mm, "mid": v(0, 135) * mm, "end": v(-15, 120) * mm});
            skLineSegment(sketch, "E85", {"start": v(80, 0) * mm, "end": v(-80, 0) * mm, "construction": true});
            skCircle(sketch, "E86.MirrorC", {"center": v(0, -120) * mm, "radius": 6 * mm});
            skLineSegment(sketch, "E87.MirrorCS", {"start": v(15, -108) * mm, "end": v(15, -120) * mm});
            skLineSegment(sketch, "E88.MirrorCS", {"start": v(-15, -108) * mm, "end": v(-15, -120) * mm});
            skArc(sketch, "E89.MirrorCS", {"start": v(15, -120) * mm, "mid": v(0, -135) * mm, "end": v(-15, -120) * mm});
            skLineSegment(sketch, "E90.MirrorCS", {"start": v(-33, -90) * mm, "end": v(-15, -108) * mm});
            skLineSegment(sketch, "E91.MirrorCS", {"start": v(33, -90) * mm, "end": v(15, -108) * mm});
            skSolve(sketch);
        }
        {
            var Q0;
            Q0=makeQuery(id+"F16.imprint","IMPRINT",FACE,{"disambiguationData":[TD([[makeQuery(id+"F16.imprint","IMPRINT",EDGE,{"derivedFrom":sQuery(id+"F16.wireOp",EDGE,"E79")}),-1.0]])]});
            var Q1;
            Q1=makeQuery(id+"F16.imprint","IMPRINT",FACE,{"disambiguationData":[TD([[makeQuery(id+"F16.imprint","IMPRINT",EDGE,{"derivedFrom":sQuery(id+"F16.wireOp",EDGE,"E86.MirrorC")}),1.0]])]});
            var Q2;
            Q2=makeQuery(id+"F16.imprint","IMPRINT",FACE,{"disambiguationData":[TD([[makeQuery(id+"F16.imprint","IMPRINT",EDGE,{"derivedFrom":makeQuery(id+"F1.opExtrude","CAP_EDGE",EDGE,{"disambiguationData":[OSD([sQuery(id+"F0.wireOp",EDGE,"E1.left")])],"isStart":true})}),-1.0]])]});
            var Q3;
            Q3=makeQuery(id+"F2.opExtrude","CAP_FACE",FACE,{"disambiguationData":[OSD([sQuery(id+"F0.wireOp",EDGE,"E12"),sQuery(id+"F0.wireOp",EDGE,"E13"),sQuery(id+"F0.wireOp",EDGE,"E14"),sQuery(id+"F0.wireOp",EDGE,"E15"),sQuery(id+"F0.wireOp",EDGE,"E17.filletArc"),sQuery(id+"F0.wireOp",EDGE,"E18.filletArc"),sQuery(id+"F0.wireOp",EDGE,"E19.filletArc"),sQuery(id+"F0.wireOp",EDGE,"E20.filletArc"),sQuery(id+"F0.wireOp",EDGE,"E25.0"),sQuery(id+"F0.wireOp",EDGE,"E25.1"),sQuery(id+"F0.wireOp",EDGE,"E25.2"),sQuery(id+"F0.wireOp",EDGE,"E25.3"),sQuery(id+"F0.wireOp",EDGE,"E25.4"),sQuery(id+"F0.wireOp",EDGE,"E25.5"),sQuery(id+"F0.wireOp",EDGE,"E25.6"),sQuery(id+"F0.wireOp",EDGE,"E25.7")])],"isStart":false});
            extrude(context, id + "F17", {"entities" : qUnion([Q0, Q1, Q2]), "endBound" : BoundingType.UP_TO_SURFACE, "depth" : 25 * mm, "endBoundEntityFace" : qUnion([Q3]), "offsetDistance" : 25 * mm});
        }
    });
